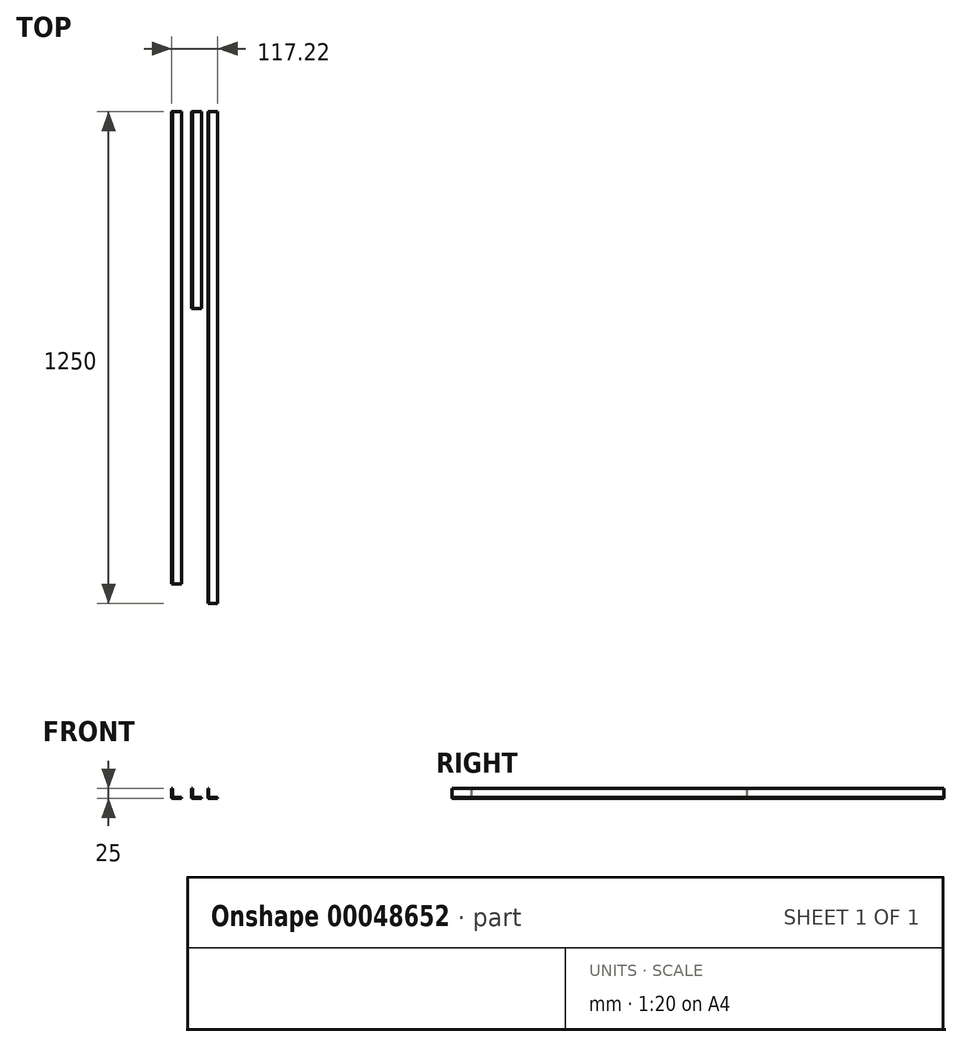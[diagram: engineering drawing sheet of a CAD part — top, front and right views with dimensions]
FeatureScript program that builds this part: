
annotation { "Feature Type Name" : "Feature", "Feature Type Description" : "" }
export const myFeature = defineFeature(function(context is Context, id is Id, definition is map)
    precondition{}
    {
        {
            var Q0;
            Q0=qCreatedBy(makeId("Front.planeOp"),FACE);
            var sketch = newSketch(context, id + "F0", { "sketchPlane" : qUnion([Q0])});
            skLineSegment(sketch, "E0", {"start": v(0, 2) * mm, "end": v(0, 25) * mm});
            skLineSegment(sketch, "E1", {"start": v(0, 25) * mm, "end": v(2, 25) * mm});
            skLineSegment(sketch, "E2", {"start": v(2, 25) * mm, "end": v(2, 4) * mm});
            skLineSegment(sketch, "E3", {"start": v(4, 2) * mm, "end": v(25, 2) * mm});
            skLineSegment(sketch, "E4", {"start": v(25, 2) * mm, "end": v(25, 0) * mm});
            skLineSegment(sketch, "E5", {"start": v(25, 0) * mm, "end": v(2, 0) * mm});
            skPoint(sketch, "E6.visualSharp", {"position": v(2, 2) * mm});
            skArc(sketch, "E6.filletArc", {"start": v(2, 4) * mm, "mid": v(2.59, 2.59) * mm, "end": v(4, 2) * mm});
            skPoint(sketch, "E7.visualSharp", {"position": v(0, 0) * mm});
            skArc(sketch, "E7.filletArc", {"start": v(0, 2) * mm, "mid": v(0.59, 0.59) * mm, "end": v(2, 0) * mm});
            skSolve(sketch);
        }
        {
            var Q0;
            Q0=makeQuery(id+"F0.imprint","IMPRINT",FACE,{"disambiguationData":[TD([[makeQuery(id+"F0.imprint","IMPRINT",EDGE,{"derivedFrom":sQuery(id+"F0.wireOp",EDGE,"E0")}),-1.0]])]});
            extrude(context, id + "F1", {"entities" : qUnion([Q0]), "depth" : 500 * mm});
        }
        {
            var Q0;
            Q0=qCreatedBy(makeId("Front.planeOp"),FACE);
            var sketch = newSketch(context, id + "F2", { "sketchPlane" : qUnion([Q0])});
            skLineSegment(sketch, "E8", {"start": v(41.22, 2) * mm, "end": v(41.22, 25) * mm});
            skLineSegment(sketch, "E9", {"start": v(41.22, 25) * mm, "end": v(43.22, 25) * mm});
            skLineSegment(sketch, "E10", {"start": v(43.22, 25) * mm, "end": v(43.22, 4) * mm});
            skLineSegment(sketch, "E11", {"start": v(45.22, 2) * mm, "end": v(66.22, 2) * mm});
            skLineSegment(sketch, "E12", {"start": v(66.22, 2) * mm, "end": v(66.22, 0) * mm});
            skLineSegment(sketch, "E13", {"start": v(66.22, 0) * mm, "end": v(43.22, 0) * mm});
            skPoint(sketch, "E14.visualSharp", {"position": v(43.22, 2) * mm});
            skArc(sketch, "E14.filletArc", {"start": v(43.22, 4) * mm, "mid": v(43.8, 2.59) * mm, "end": v(45.22, 2) * mm});
            skPoint(sketch, "E15.visualSharp", {"position": v(41.22, 0) * mm});
            skArc(sketch, "E15.filletArc", {"start": v(41.22, 2) * mm, "mid": v(41.8, 0.59) * mm, "end": v(43.22, 0) * mm});
            skSolve(sketch);
        }
        {
            var Q0;
            Q0=makeQuery(id+"F2.imprint","IMPRINT",FACE,{"disambiguationData":[TD([[makeQuery(id+"F2.imprint","IMPRINT",EDGE,{"derivedFrom":sQuery(id+"F2.wireOp",EDGE,"E8")}),-1.0]])]});
            extrude(context, id + "F3", {"entities" : qUnion([Q0]), "depth" : 1250 * mm});
        }
        {
            var Q0;
            Q0=qCreatedBy(makeId("Front.planeOp"),FACE);
            var sketch = newSketch(context, id + "F4", { "sketchPlane" : qUnion([Q0])});
            skLineSegment(sketch, "E16", {"start": v(-51, 2) * mm, "end": v(-51, 25) * mm});
            skLineSegment(sketch, "E17", {"start": v(-51, 25) * mm, "end": v(-49, 25) * mm});
            skLineSegment(sketch, "E18", {"start": v(-49, 25) * mm, "end": v(-49, 4) * mm});
            skLineSegment(sketch, "E19", {"start": v(-47, 2) * mm, "end": v(-26, 2) * mm});
            skLineSegment(sketch, "E20", {"start": v(-26, 2) * mm, "end": v(-26, 0) * mm});
            skLineSegment(sketch, "E21", {"start": v(-26, 0) * mm, "end": v(-49, 0) * mm});
            skPoint(sketch, "E22.visualSharp", {"position": v(-49, 2) * mm});
            skArc(sketch, "E22.filletArc", {"start": v(-49, 4) * mm, "mid": v(-48.42, 2.59) * mm, "end": v(-47, 2) * mm});
            skPoint(sketch, "E23.visualSharp", {"position": v(-51, 0) * mm});
            skArc(sketch, "E23.filletArc", {"start": v(-51, 2) * mm, "mid": v(-50.42, 0.59) * mm, "end": v(-49, 0) * mm});
            skSolve(sketch);
        }
        {
            var Q0;
            Q0=makeQuery(id+"F4.imprint","IMPRINT",FACE,{"disambiguationData":[TD([[makeQuery(id+"F4.imprint","IMPRINT",EDGE,{"derivedFrom":sQuery(id+"F4.wireOp",EDGE,"E16")}),-1.0]])]});
            extrude(context, id + "F5", {"entities" : qUnion([Q0]), "depth" : 1200 * mm});
        }
    });
